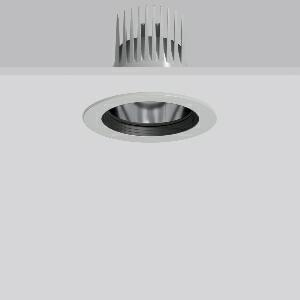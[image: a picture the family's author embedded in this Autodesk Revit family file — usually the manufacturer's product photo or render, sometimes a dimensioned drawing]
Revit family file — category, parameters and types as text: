
# Revit family: heledon_maxi_e_901777_004_d266
name_source: partatom
category: Lighting Fixtures
units: mm (PartAtom-declared; Revit-internal decimal feet)

## family parameters
Cut with Voids When Loaded = No
Host = Face
Light Source = No
Part Type = Normal
Room Calculation Point = No
Round Connector Dimension = Use Diameter
Shared = No

## types (1)
- HELEDON maxi E (1 x LED Modul 920 meat+, 2200 lm, 2000)
    Apparent Load = 33 VA
    Approval mark = CE
    CIE Flux Codes = 100 100 100 100 100
    Color Rendering = 90
    Color Temperature = 2000
    Default Elevation = 1800 mm
    Description = Series: HELEDON maxi
Round recessed downlight. Housing: die-cast aluminium, powder-coated. Black plastic ring and recessed LED to prevent glare from the side. Optical assembly with reflector made of MIRO-Silver with 98% total light reflection for outstanding efficiency - can be changed without tools. Special LED for illumination of meat included. Suitable for Recessed ceiling mounting. Installation without tools thanks to spring fastening system. Including separate LED converter with connecting cable 600 mm.High quality converter without flickering and stroboscopic effect. Through-wiring box (5 pole) available as accessory. The following accessories can be mounted without use of tools: interchangeable lenses, decorative glasses, honeycomb louvre, clear and frosted diffusers, white interchangeable plastic ring. 
Colour: silver
Diameter: 162 mm
Height: 3 mm
Cut-out diameter: 152 mm
Recess height: 200 mm
Luminaire: recess height: 135 mm
Lamp: LED
Socket: without socket
Colour temperature: meat +
System power: 33 W
Rated luminous flux: 2200 lm
Luminous efficiency: 67 lm/W
Control gear: Regulated power supply
Protection class: II
Type of protection: IP 20
    Height = 0 mm  [stored 0 ft]
    Lamp = 1 x LED Modul 920 meat+
    Lamp Light Flux = 2200 lm
    Lamp count = 1
    Length = 162 mm
    Lifetime = 50000 h
    Luminous efficacy = 67 lm/W
    Manufacturer = RZB
    ModVariant = No
    Model = 901777.004
    Mounting Place = Ceiling
    Mounting Type = Recessed
    Number of Poles = 1
    OnlyDefault = Yes
    Power Factor = 1
    Product Name = HELEDON maxi E
    Product group = Recessed downlights
    ProductGroupID = 402
    Protection Class = Protection class II
    Protection Degree = IP 20
    RLX_Detail_Level = 1
    RLX_Emergency_Light_Flux = 0 lm
    RLX_Emergency_Type = 0
    RLX_Emergency_Type_DB = No
    RlxData = <blob elided: 119429 chars, md5=d64f1148>
    Socket = socket
    Standby Power = 0 W
    System Light Flux = 2200 lm
    System Power = 33 W
    Type Comments = Product without accessories
    Type Image = 901662.004.jpg
    URL = http://relux.com
    VarID = ---
    Voltage = 230 V
    Voltage Range = 220-240 V
    Weight = 0.00 kg
    Width = 0 mm  [stored 0 ft]

note: [stored X ft] marks values corroborated as IEEE doubles in the binary element streams (Revit-internal decimal feet)

## geometry (parser evidence)
native form markers: Blend x4, Sweep x11
no freeform markers — native parametric forms only
